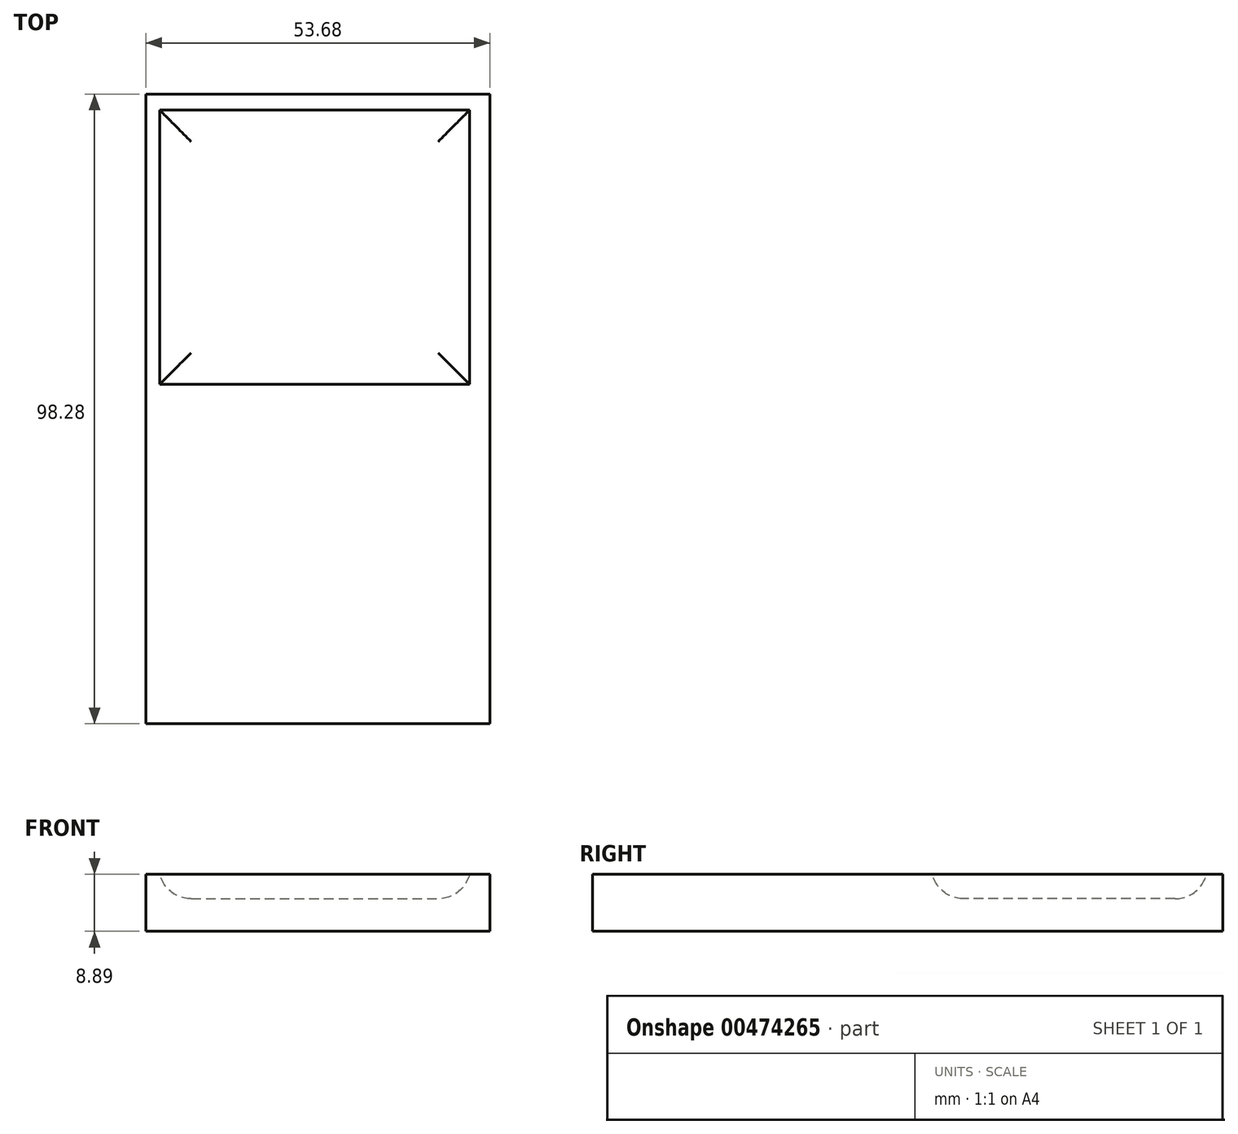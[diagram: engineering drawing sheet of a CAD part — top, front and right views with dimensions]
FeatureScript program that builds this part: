
annotation { "Feature Type Name" : "Feature", "Feature Type Description" : "" }
export const myFeature = defineFeature(function(context is Context, id is Id, definition is map)
    precondition{}
    {
        {
            var Q0;
            Q0=qCreatedBy(makeId("Top.planeOp"),FACE);
            var sketch = newSketch(context, id + "F0", { "sketchPlane" : qUnion([Q0])});
            skLineSegment(sketch, "E0.bottom", {"start": v(-26.84, 49.14) * mm, "end": v(26.84, 49.14) * mm});
            skLineSegment(sketch, "E0.top", {"start": v(-26.84, -49.14) * mm, "end": v(26.84, -49.14) * mm});
            skLineSegment(sketch, "E0.left", {"start": v(-26.84, 49.14) * mm, "end": v(-26.84, -49.14) * mm});
            skLineSegment(sketch, "E0.right", {"start": v(26.84, 49.14) * mm, "end": v(26.84, -49.14) * mm});
            skLineSegment(sketch, "E1", {"start": v(-26.84, 0) * mm, "end": v(26.84, 0) * mm, "construction": true});
            skLineSegment(sketch, "E2", {"start": v(0, 49.14) * mm, "end": v(0, -49.14) * mm, "construction": true});
            skSolve(sketch);
        }
        {
            var Q0;
            Q0 = qSketchRegion(id + "F0", true);
            extrude(context, id + "F1", {"entities" : qUnion([Q0]), "oppositeDirection" : true, "depth" : 8.9 * mm});
        }
        {
            var Q0;
            Q0=qCreatedBy(makeId("Top.planeOp"),FACE);
            var sketch = newSketch(context, id + "F2", { "sketchPlane" : qUnion([Q0])});
            skLineSegment(sketch, "E3.bottom", {"start": v(-24.67, 46.62) * mm, "end": v(23.66, 46.62) * mm});
            skLineSegment(sketch, "E3.top", {"start": v(-24.67, 3.84) * mm, "end": v(23.66, 3.84) * mm});
            skLineSegment(sketch, "E3.left", {"start": v(-24.67, 46.62) * mm, "end": v(-24.67, 3.84) * mm});
            skLineSegment(sketch, "E3.right", {"start": v(23.66, 46.62) * mm, "end": v(23.66, 3.84) * mm});
            skSolve(sketch);
        }
        {
            var Q0;
            Q0 = qSketchRegion(id + "F2", true);
            extrude(context, id + "F3", {"entities" : qUnion([Q0]), "operationType" : NewBodyOperationType.REMOVE, "oppositeDirection" : true, "depth" : 3.8 * mm});
        }
        {
            var Q0;
            Q0=makeQuery(id+"F3.boolean.opBoolean","COPY",FACE,{"derivedFrom":makeQuery(id+"F3.opExtrude","CAP_FACE",FACE,{"disambiguationData":[OSD([sQuery(id+"F2.wireOp",EDGE,"E3.bottom"),sQuery(id+"F2.wireOp",EDGE,"E3.top"),sQuery(id+"F2.wireOp",EDGE,"E3.left"),sQuery(id+"F2.wireOp",EDGE,"E3.right")])],"isStart":false})});
            fillet(context, id + "F4", {"entities" : qUnion([Q0]), "radius" : 5.08 * mm, "tangentPropagation" : true, "allowEdgeOverflow" : false});
        }
    });
